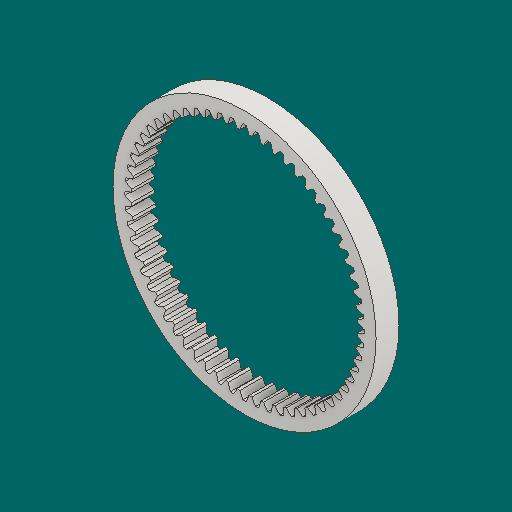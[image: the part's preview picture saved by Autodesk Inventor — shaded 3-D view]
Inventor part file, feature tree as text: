
AUTODESK INVENTOR PART (.ipt)
format: ipt  version: 2023.1 (Build 271208000, 208)  size: 450,560 bytes
history: native  units: in
note: dims shown in document units (in); Inventor stores cm internally (conversion verified against a paired STEP export)
features: other x12, plane x3, sketch x2
ambient origin geometry x8: Origin, YZ Plane, XZ Plane, XY Plane, X Axis, Y Axis, Z Axis, Center Point
bodies: Solid1 (feature_tree)
feature tree (17):
  other  "Spur Gear2"
  other  "Solid1::Spur Gear2"
  other  "TaggingFeature1"
  sketch  "Sketch1"  dims[d0=0.3937in]
  sketch  "Sketch2"  dims[d9=0.0in d14=0.0in d15=1.05in d16=0.0in d17=0.0in d18=0.0in d19=1.05in]
  plane  "XZ Plane_1"
  plane  "Work Plane2"
  plane  "Work Plane3"
  other  "Srf1"
  other  "Srf1::Derived"
  other  "Start plane iMate"
  other  "Distance iMate"
  other  "Mesh iMate"
  other  "Position iMate"
  other  "Axis iMate"
  other  "Mesh iMate2"
  other  "Align iMate"
